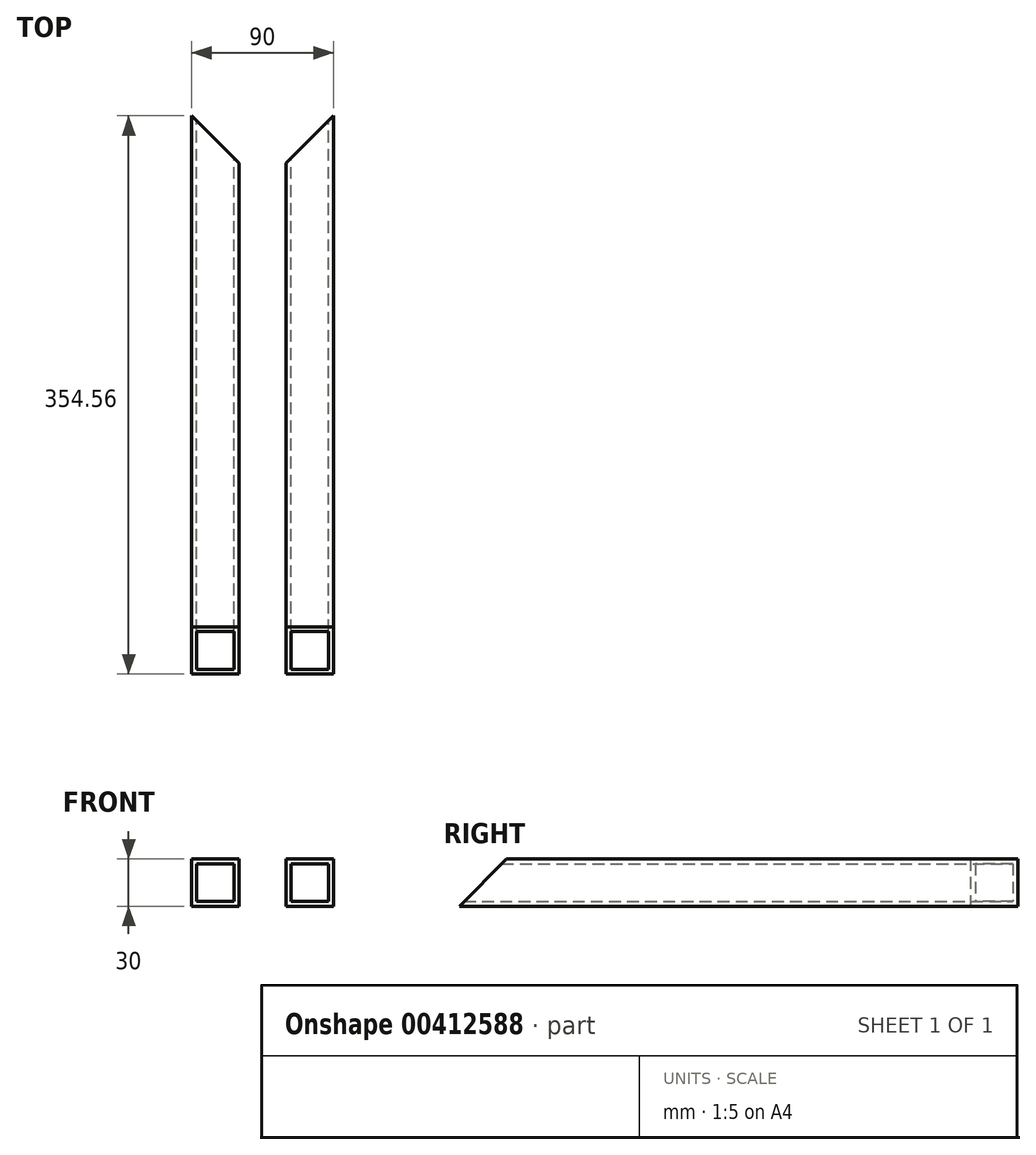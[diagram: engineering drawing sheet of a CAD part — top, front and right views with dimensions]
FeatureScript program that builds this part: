
annotation { "Feature Type Name" : "Feature", "Feature Type Description" : "" }
export const myFeature = defineFeature(function(context is Context, id is Id, definition is map)
    precondition{}
    {
        {
            assignVariable(context, id + "F0", {"name" : "BeamWidth", "anyValue" : 30});
        }
        {
            assignVariable(context, id + "F1", {"name" : "EdgeCircle", "anyValue" : 530});
        }
        {
            assignVariable(context, id + "F2", {"name" : "Diagonal", "anyValue" : getVariable(context, 'EdgeCircle') * 0.87});
        }
        {
            assignVariable(context, id + "F3", {"name" : "BeamEdgeLength", "anyValue" : getVariable(context, 'Diagonal') / 1.41});
        }
        {
            assignVariable(context, id + "F4", {"name" : "BeamOutsideLength", "anyValue" : getVariable(context, 'BeamEdgeLength') + getVariable(context, 'BeamWidth')});
        }
        {
            var Q0;
            Q0=qCreatedBy(makeId("Front.planeOp"),FACE);
            var sketch = newSketch(context, id + "F5", { "sketchPlane" : qUnion([Q0])});
            skLineSegment(sketch, "E0.bottom", {"start": v(15, -15) * mm, "end": v(-15, -15) * mm});
            skLineSegment(sketch, "E0.top", {"start": v(15, 15) * mm, "end": v(-15, 15) * mm});
            skLineSegment(sketch, "E0.left", {"start": v(15, -15) * mm, "end": v(15, 15) * mm});
            skLineSegment(sketch, "E0.right", {"start": v(-15, -15) * mm, "end": v(-15, 15) * mm});
            skPoint(sketch, "E0.middle", {"position": v(0, 0) * mm});
            skLineSegment(sketch, "E1.bottom", {"start": v(12, 12) * mm, "end": v(-12, 12) * mm});
            skLineSegment(sketch, "E1.top", {"start": v(12, -12) * mm, "end": v(-12, -12) * mm});
            skLineSegment(sketch, "E1.left", {"start": v(12, 12) * mm, "end": v(12, -12) * mm});
            skLineSegment(sketch, "E1.right", {"start": v(-12, 12) * mm, "end": v(-12, -12) * mm});
            skSolve(sketch);
        }
        {
            var Q0;
            Q0 = qSketchRegion(id + "F5", true);
            extrude(context, id + "F6", {"entities" : qUnion([Q0]), "depth" : (getVariable(context, 'BeamOutsideLength')) * mm, "symmetric" : true});
        }
        {
            var Q0;
            Q0=makeQuery(id+"F6.opExtrude","SWEPT_BODY",BODY,{"disambiguationData":[OSD([sQuery(id+"F5.wireOp",EDGE,"E0.bottom"),sQuery(id+"F5.wireOp",EDGE,"E0.top"),sQuery(id+"F5.wireOp",EDGE,"E0.left"),sQuery(id+"F5.wireOp",EDGE,"E0.right")])]});
            transform(context, id + "F7", {"entities" : qUnion([Q0]), "transformType" : TransformType.TRANSLATION_3D, "dx" : (getVariable(context, 'BeamWidth') * 2) * mm, "dy" : 0 * mm, "dz" : 0 * mm, "makeCopy" : true});
        }
        {
            var Q0;
            Q0=makeQuery(id+"F6.opExtrude","CAP_EDGE",EDGE,{"disambiguationData":[OSD([sQuery(id+"F5.wireOp",EDGE,"E0.top")])],"isStart":false});
            var Q1;
            Q1=makeQuery(id+"F6.opExtrude","CAP_EDGE",EDGE,{"disambiguationData":[OSD([sQuery(id+"F5.wireOp",EDGE,"E0.left")])],"isStart":true});
            var Q2;
            Q2=makeQuery(id+"F7.opPattern","COPY",EDGE,{"derivedFrom":makeQuery(id+"F6.opExtrude","CAP_EDGE",EDGE,{"disambiguationData":[OSD([sQuery(id+"F5.wireOp",EDGE,"E0.top")])],"isStart":false}),"instanceName":"1"});
            var Q3;
            Q3=makeQuery(id+"F7.opPattern","COPY",EDGE,{"derivedFrom":makeQuery(id+"F6.opExtrude","CAP_EDGE",EDGE,{"disambiguationData":[OSD([sQuery(id+"F5.wireOp",EDGE,"E0.right")])],"isStart":true}),"instanceName":"1"});
            chamfer(context, id + "F8", {"entities" : qUnion([Q0, Q1, Q2, Q3]), "width" : (getVariable(context, 'BeamWidth')) * mm, "tangentPropagation" : true});
        }
    });
